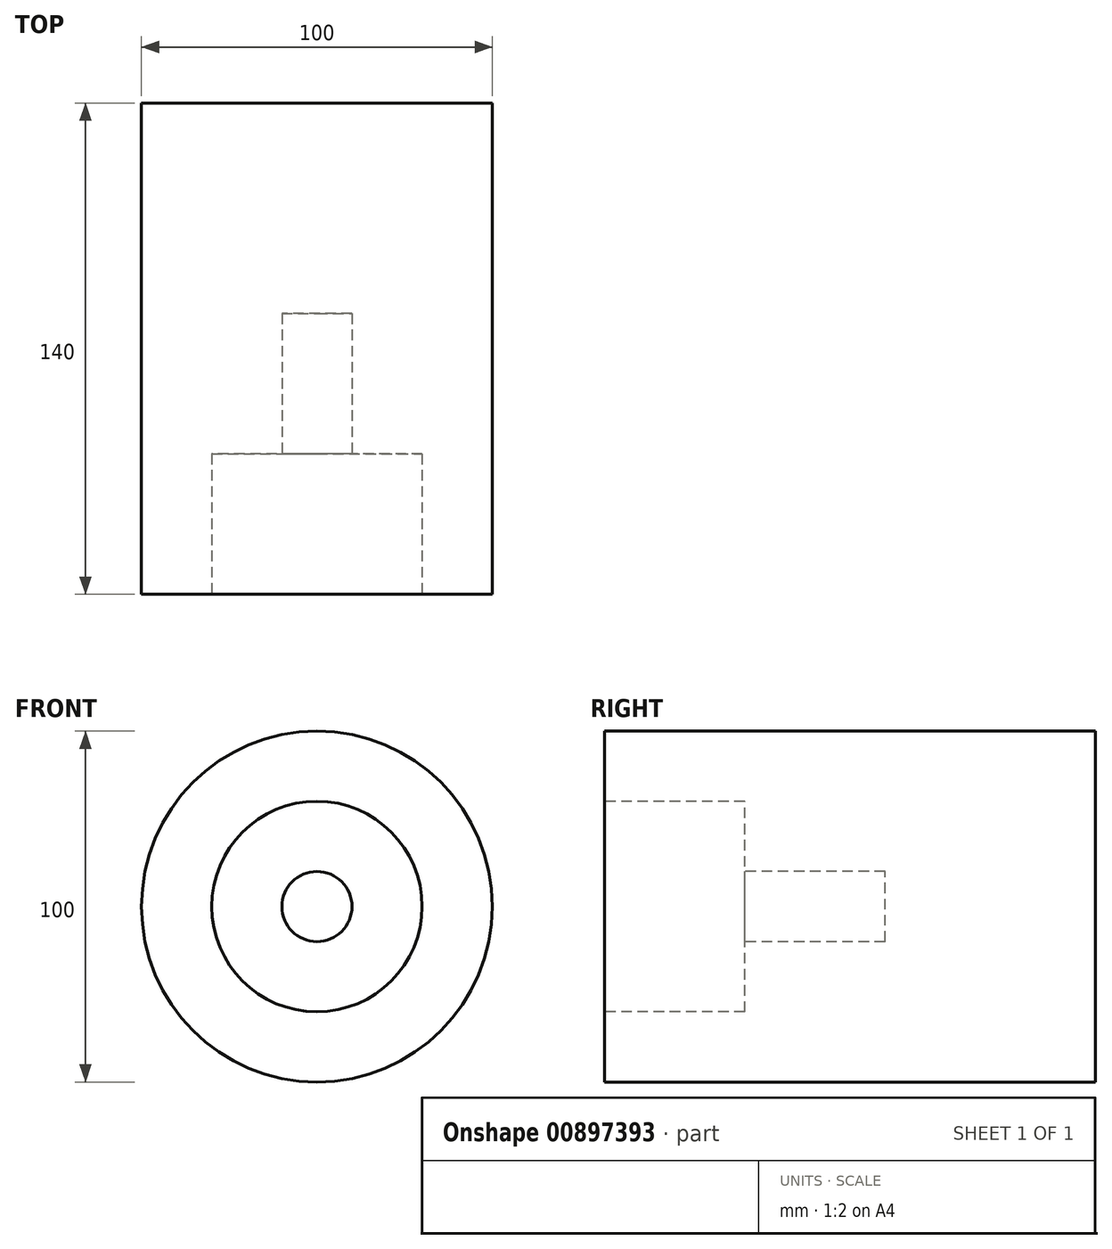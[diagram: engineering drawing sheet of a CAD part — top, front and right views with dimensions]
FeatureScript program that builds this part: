
annotation { "Feature Type Name" : "Feature", "Feature Type Description" : "" }
export const myFeature = defineFeature(function(context is Context, id is Id, definition is map)
    precondition{}
    {
        {
            var Q0;
            Q0=qCreatedBy(makeId("Front.planeOp"),FACE);
            var sketch = newSketch(context, id + "F0", { "sketchPlane" : qUnion([Q0])});
            skCircle(sketch, "E0", {"center": v(0, 0) * mm, "radius": 50 * mm});
            skSolve(sketch);
        }
        {
            var Q0;
            Q0 = qSketchRegion(id + "F0", true);
            extrude(context, id + "F1", {"entities" : qUnion([Q0]), "oppositeDirection" : true, "depth" : 140 * mm, "offsetDistance" : 25.4 * mm});
        }
        {
            var Q0;
            Q0=makeQuery(id+"F1.opExtrude","CAP_FACE",FACE,{"disambiguationData":[OSD([sQuery(id+"F0.wireOp",EDGE,"E0")])],"isStart":true});
            var sketch = newSketch(context, id + "F2", { "sketchPlane" : qUnion([Q0])});
            skCircle(sketch, "E1", {"center": v(0, 0) * mm, "radius": 30 * mm});
            skSolve(sketch);
        }
        {
            var Q0;
            Q0 = qSketchRegion(id + "F2", true);
            extrude(context, id + "F3", {"entities" : qUnion([Q0]), "operationType" : NewBodyOperationType.REMOVE, "oppositeDirection" : true, "depth" : 40 * mm, "offsetDistance" : 25.4 * mm});
        }
        {
            var Q0;
            Q0=makeQuery(id+"F2.imprint","IMPRINT",FACE,{"disambiguationData":[TD([[makeQuery(id+"F2.imprint","IMPRINT",EDGE,{"derivedFrom":sQuery(id+"F2.wireOp",EDGE,"E1")}),1.0]])]});
            var sketch = newSketch(context, id + "F4", { "sketchPlane" : qUnion([Q0])});
            skCircle(sketch, "E2", {"center": v(0, 0) * mm, "radius": 10 * mm});
            skSolve(sketch);
        }
        {
            var Q0;
            Q0 = qSketchRegion(id + "F4", true);
            extrude(context, id + "F5", {"entities" : qUnion([Q0]), "operationType" : NewBodyOperationType.REMOVE, "oppositeDirection" : true, "depth" : 80 * mm, "offsetDistance" : 25.4 * mm});
        }
    });
